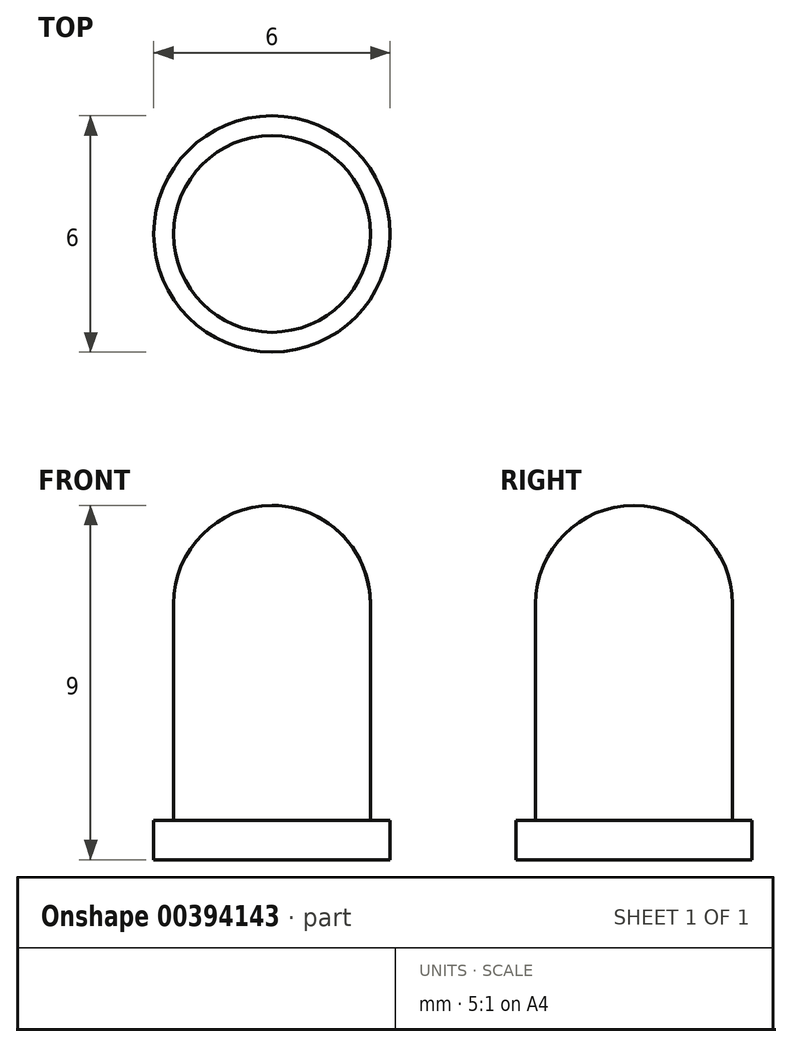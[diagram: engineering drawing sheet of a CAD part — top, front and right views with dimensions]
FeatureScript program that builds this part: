
annotation { "Feature Type Name" : "Feature", "Feature Type Description" : "" }
export const myFeature = defineFeature(function(context is Context, id is Id, definition is map)
    precondition{}
    {
        {
            var Q0;
            Q0=qCreatedBy(makeId("Top.planeOp"),FACE);
            var sketch = newSketch(context, id + "F0", { "sketchPlane" : qUnion([Q0])});
            skCircle(sketch, "E0", {"center": v(0, 0) * mm, "radius": 3 * mm});
            skSolve(sketch);
        }
        {
            var Q0;
            Q0=qSketchRegion(id+"F0",true);
            extrude(context, id + "F1", {"entities" : qUnion([Q0]), "depth" : 1 * mm});
        }
        {
            var Q0;
            Q0=makeQuery(id+"F1.opExtrude","CAP_FACE",FACE,{"disambiguationData":[OSD([sQuery(id+"F0.wireOp",EDGE,"E0")])],"isStart":false});
            var sketch = newSketch(context, id + "F2", { "sketchPlane" : qUnion([Q0])});
            skCircle(sketch, "E1", {"center": v(0, 0) * mm, "radius": 2.5 * mm});
            skSolve(sketch);
        }
        {
            var Q0;
            Q0=makeQuery(id+"F2.imprint","IMPRINT",FACE,{"disambiguationData":[TD([[makeQuery(id+"F2.imprint","IMPRINT",EDGE,{"derivedFrom":sQuery(id+"F2.wireOp",EDGE,"E1")}),1.0]])]});
            extrude(context, id + "F3", {"entities" : qUnion([Q0]), "operationType" : NewBodyOperationType.ADD, "depth" : 8 * mm});
        }
        {
            var Q0;
            Q0=makeQuery(id+"F3.opExtrude","CAP_EDGE",EDGE,{"disambiguationData":[OSD([sQuery(id+"F2.wireOp",EDGE,"E1")])],"isStart":false});
            fillet(context, id + "F4", {"entities" : qUnion([Q0]), "radius" : 2.5 * mm, "tangentPropagation" : true, "allowEdgeOverflow" : false});
        }
    });
